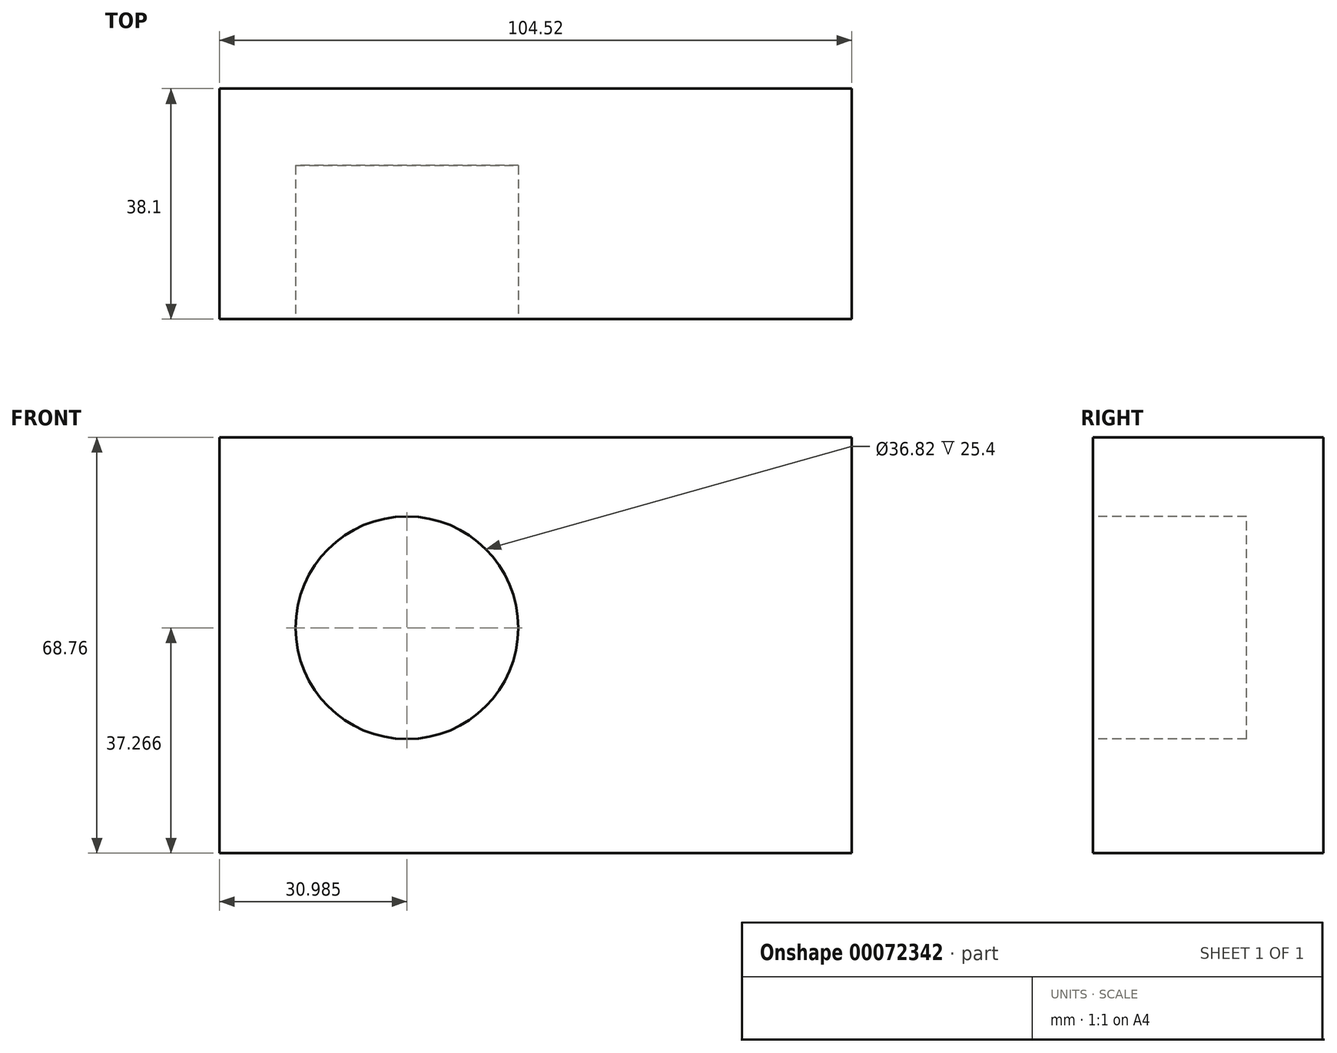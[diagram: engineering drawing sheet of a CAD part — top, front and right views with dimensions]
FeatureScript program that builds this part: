
annotation { "Feature Type Name" : "Feature", "Feature Type Description" : "" }
export const myFeature = defineFeature(function(context is Context, id is Id, definition is map)
    precondition{}
    {
        {
            var Q0;
            Q0=qCreatedBy(makeId("Front.planeOp"),FACE);
            var sketch = newSketch(context, id + "F0", { "sketchPlane" : qUnion([Q0])});
            skLineSegment(sketch, "E0", {"start": v(-57.33, -23.78) * mm, "end": v(47.2, -23.78) * mm});
            skLineSegment(sketch, "E1", {"start": v(47.2, -23.78) * mm, "end": v(47.2, 44.98) * mm});
            skLineSegment(sketch, "E2", {"start": v(47.2, 44.98) * mm, "end": v(-57.33, 44.98) * mm});
            skLineSegment(sketch, "E3", {"start": v(-57.33, 44.98) * mm, "end": v(-57.33, -23.78) * mm});
            skSolve(sketch);
        }
        {
            var Q0;
            Q0=makeQuery(id+"F0.imprint","IMPRINT",FACE,{"disambiguationData":[TD([[makeQuery(id+"F0.imprint","IMPRINT",EDGE,{"derivedFrom":sQuery(id+"F0.wireOp",EDGE,"E0")}),1.0]])]});
            extrude(context, id + "F1", {"entities" : qUnion([Q0]), "depth" : 38.1 * mm});
        }
        {
            var Q0;
            Q0=makeQuery(id+"F1.opExtrude","CAP_FACE",FACE,{"disambiguationData":[OSD([sQuery(id+"F0.wireOp",EDGE,"E0"),sQuery(id+"F0.wireOp",EDGE,"E1"),sQuery(id+"F0.wireOp",EDGE,"E2"),sQuery(id+"F0.wireOp",EDGE,"E3")])],"isStart":false});
            var sketch = newSketch(context, id + "F2", { "sketchPlane" : qUnion([Q0])});
            skCircle(sketch, "E4", {"center": v(-26.35, 13.49) * mm, "radius": 18.4 * mm});
            skSolve(sketch);
        }
        {
            var Q0;
            Q0=makeQuery(id+"F2.imprint","IMPRINT",FACE,{"disambiguationData":[TD([[makeQuery(id+"F2.imprint","IMPRINT",EDGE,{"derivedFrom":sQuery(id+"F2.wireOp",EDGE,"E4")}),1.0]])]});
            extrude(context, id + "F3", {"entities" : qUnion([Q0]), "operationType" : NewBodyOperationType.REMOVE, "oppositeDirection" : true, "depth" : 25.4 * mm});
        }
    });
